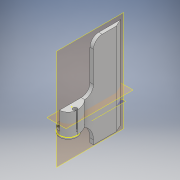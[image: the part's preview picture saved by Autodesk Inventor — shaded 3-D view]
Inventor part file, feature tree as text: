
AUTODESK INVENTOR PART (.ipt)
format: ipt  version: 2018 (Build 220112000, 112)  size: 511,488 bytes
history: native  units: mm
features: extrude x13, sketch x13, projected_geometry x4, fillet x2, plane x2, other x1
ambient origin geometry x8: Origin, YZ Plane, XZ Plane, XY Plane, X Axis, Y Axis, Z Axis, Center Point
bodies: Solid1 (feature_tree)
feature tree (35):
  extrude  "Extrusion1"  Depth=3.556mm
  extrude  "Extrusion2"  Depth=3.556mm
  extrude  "Extrusion3"  Depth=44.45mm
  fillet  "Fillet1"  Radius=31.75mm
  fillet  "Fillet2"  Radius=44.45mm
  extrude  "Extrusion4"  Depth=5.08mm TaperAngle=0.0deg
  extrude  "Extrusion5"  Depth=12.7mm
  sketch  "Sketch8"  dims[d15=25.4mm d16=5.08mm d17=0.0mm]
  sketch  "Sketch9"  dims[d19=5.08mm d20=0.0mm d49=6.35mm d50=0.0mm]
  extrude  "Extrusion6"  Depth=5.08mm TaperAngle=0.0deg
  extrude  "Extrusion7"  Depth=6.35mm TaperAngle=0.0deg
  extrude  "Extrusion8"  Depth=6.0mm
  plane  "Work Plane2"
  sketch  "Sketch12"  dims[d57=31.75mm d58=2.54mm d59=0.0mm]
  extrude  "Extrusion9"  [1 undecoded]
  extrude  "Extrusion10"  Depth=2.54mm TaperAngle=0.0deg
  extrude  "Extrusion11"  Depth=5.08mm TaperAngle=0.0deg
  extrude  "Extrusion12"  Depth=6.0mm
  extrude  "Extrusion13"  [1 undecoded]
  sketch  "Sketch1"  dims[d0=3.556mm d1=3.556mm]
  sketch  "Sketch2"  dims[d2=3.556mm d3=3.556mm]
  sketch  "Sketch3"  dims[d4=25.4mm d5=0.0mm d6=44.45mm d7=31.75mm d8=44.45mm]
  sketch  "Sketch6"  dims[d9=133.35mm d10=5.08mm d11=0.0mm]
  sketch  "Sketch7"  dims[d12=5.08mm d13=0.0mm d14=12.7mm]
  projected_geometry  "Projected Loop1"
  sketch  "Sketch10"  dims[d51=6.35mm d52=0.0mm d53=6.0mm]
  projected_geometry  "Projected Loop2"
  sketch  "Sketch11"  dims[d54=30.48mm d55=0.0mm d56=-31.75mm]
  plane  "Work Plane1"
  projected_geometry  "Projected Loop3"
  sketch  "Sketch13"  dims[d60=5.08mm d61=0.0mm d62=5.08mm d63=0.0mm]
  sketch  "Sketch14"  dims[d64=5.08mm d65=0.0mm d66=6.0mm]
  sketch  "Sketch15"  dims[d67=5.08mm d68=0.0mm]
  projected_geometry  "Projected Loop4"
  other  "Cavity1"
note: 2 required parameter values undecoded (feature->parameter linkage not recoverable at this tier; creation-order binding heuristic only, values carry confidence <= 0.55)
